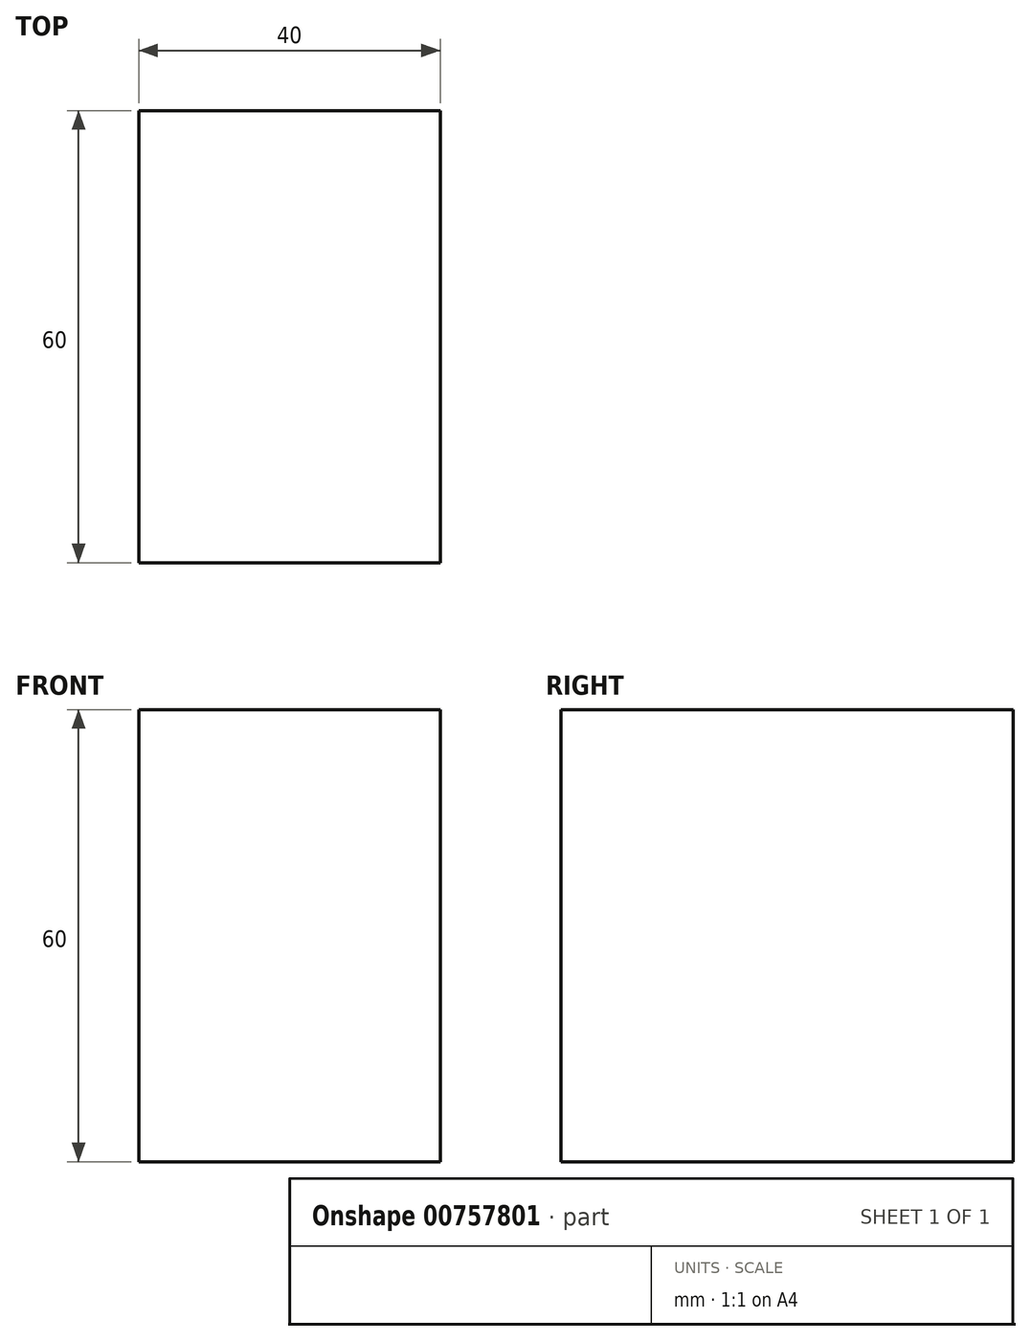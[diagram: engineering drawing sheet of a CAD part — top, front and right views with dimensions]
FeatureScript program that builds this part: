
annotation { "Feature Type Name" : "Feature", "Feature Type Description" : "" }
export const myFeature = defineFeature(function(context is Context, id is Id, definition is map)
    precondition{}
    {
        {
            var Q0;
            Q0=qCreatedBy(makeId("Front.planeOp"),FACE);
            var sketch = newSketch(context, id + "F0", { "sketchPlane" : qUnion([Q0])});
            skLineSegment(sketch, "E0.bottom", {"start": v(0, 0) * mm, "end": v(40, 0) * mm});
            skLineSegment(sketch, "E0.top", {"start": v(0, 60) * mm, "end": v(40, 60) * mm});
            skLineSegment(sketch, "E0.left", {"start": v(0, 0) * mm, "end": v(0, 60) * mm});
            skLineSegment(sketch, "E0.right", {"start": v(40, 0) * mm, "end": v(40, 60) * mm});
            skSolve(sketch);
        }
        {
            var Q0;
            Q0=makeQuery(id+"F0.imprint","IMPRINT",FACE,{"disambiguationData":[TD([[makeQuery(id+"F0.imprint","IMPRINT",EDGE,{"derivedFrom":sQuery(id+"F0.wireOp",EDGE,"E0.bottom")}),1.0]])]});
            extrude(context, id + "F1", {"entities" : qUnion([Q0]), "depth" : 60 * mm, "offsetDistance" : 25 * mm});
        }
    });
